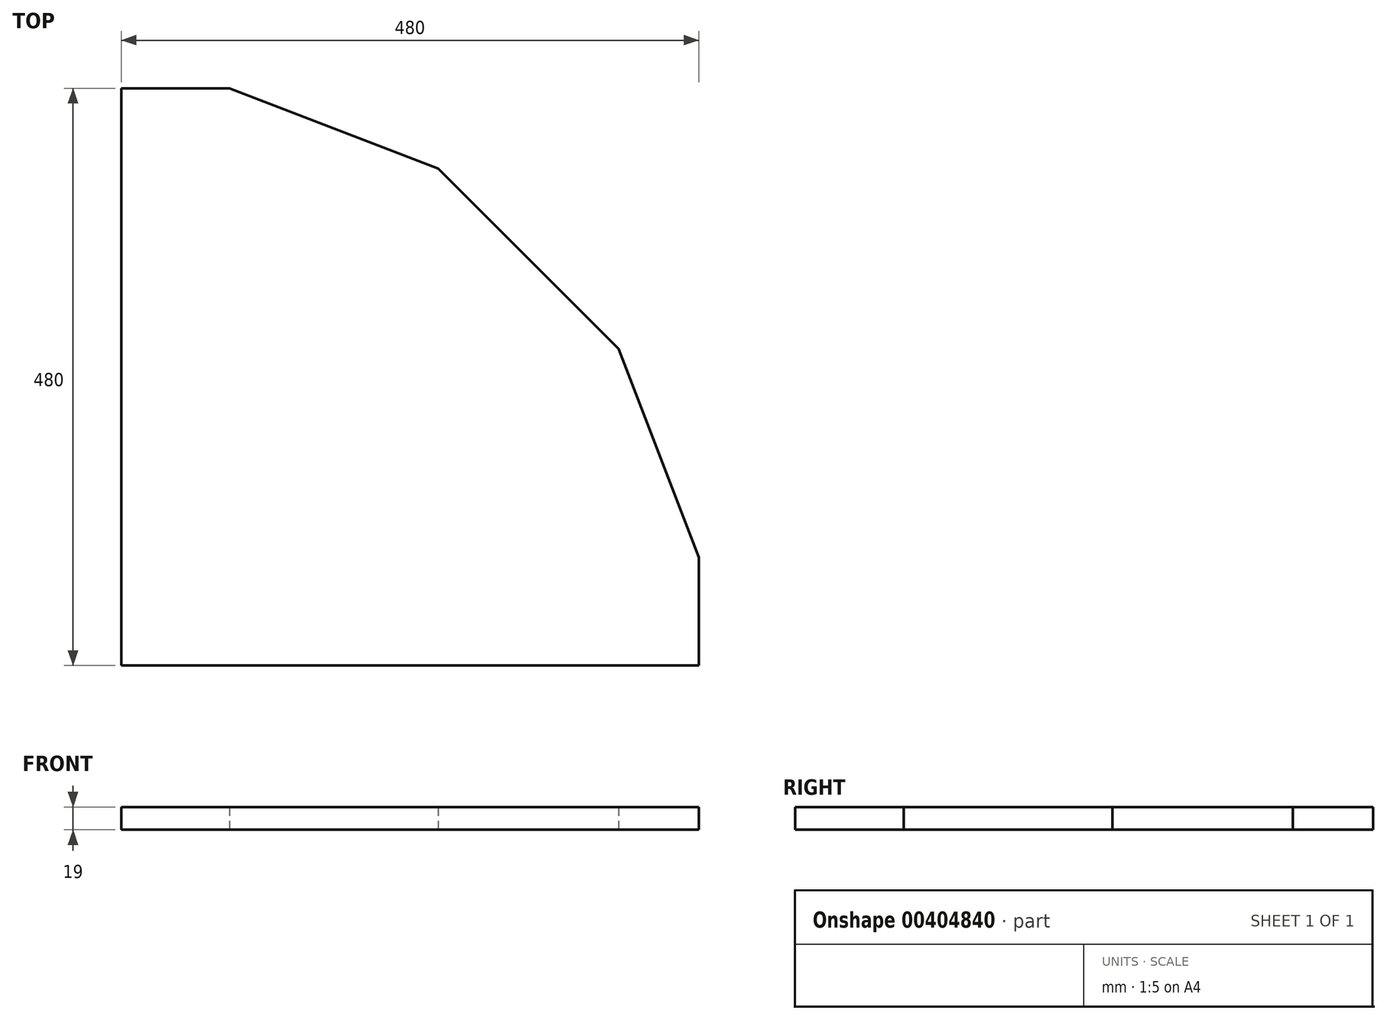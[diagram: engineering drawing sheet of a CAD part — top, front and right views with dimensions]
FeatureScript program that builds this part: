
annotation { "Feature Type Name" : "Feature", "Feature Type Description" : "" }
export const myFeature = defineFeature(function(context is Context, id is Id, definition is map)
    precondition{}
    {
        {
            var Q0;
            Q0=qCreatedBy(makeId("Top.planeOp"),FACE);
            var sketch = newSketch(context, id + "F0", { "sketchPlane" : qUnion([Q0])});
            skLineSegment(sketch, "E0.bottom", {"start": v(-240, 240) * mm, "end": v(-150, 240) * mm});
            skLineSegment(sketch, "E0.top", {"start": v(-240, -240) * mm, "end": v(240, -240) * mm});
            skLineSegment(sketch, "E0.left", {"start": v(-240, 240) * mm, "end": v(-240, -240) * mm});
            skLineSegment(sketch, "E0.right", {"start": v(240, -150) * mm, "end": v(240, -240) * mm});
            skPoint(sketch, "E0.middle", {"position": v(0, 0) * mm});
            skPoint(sketch, "E1", {"position": v(23.33, 173.33) * mm});
            skPoint(sketch, "E2", {"position": v(173.33, 23.33) * mm});
            skLineSegment(sketch, "E3", {"start": v(23.33, 173.33) * mm, "end": v(173.33, 23.33) * mm});
            skPoint(sketch, "E4", {"position": v(-150, 240) * mm});
            skPoint(sketch, "E5", {"position": v(240, -150) * mm});
            skLineSegment(sketch, "E6", {"start": v(-150, 240) * mm, "end": v(23.33, 173.33) * mm});
            skLineSegment(sketch, "E7", {"start": v(173.33, 23.33) * mm, "end": v(240, -150) * mm});
            skLineSegment(sketch, "E8", {"start": v(-150, 240) * mm, "end": v(224.1, 240) * mm, "construction": true});
            skPoint(sketch, "E9", {"position": v(23.33, 240) * mm});
            skPoint(sketch, "E10", {"position": v(-240, 173.33) * mm});
            skSolve(sketch);
        }
        {
            var Q0;
            Q0 = qSketchRegion(id + "F0", true);
            extrude(context, id + "F1", {"entities" : qUnion([Q0]), "depth" : 19 * mm});
        }
    });
